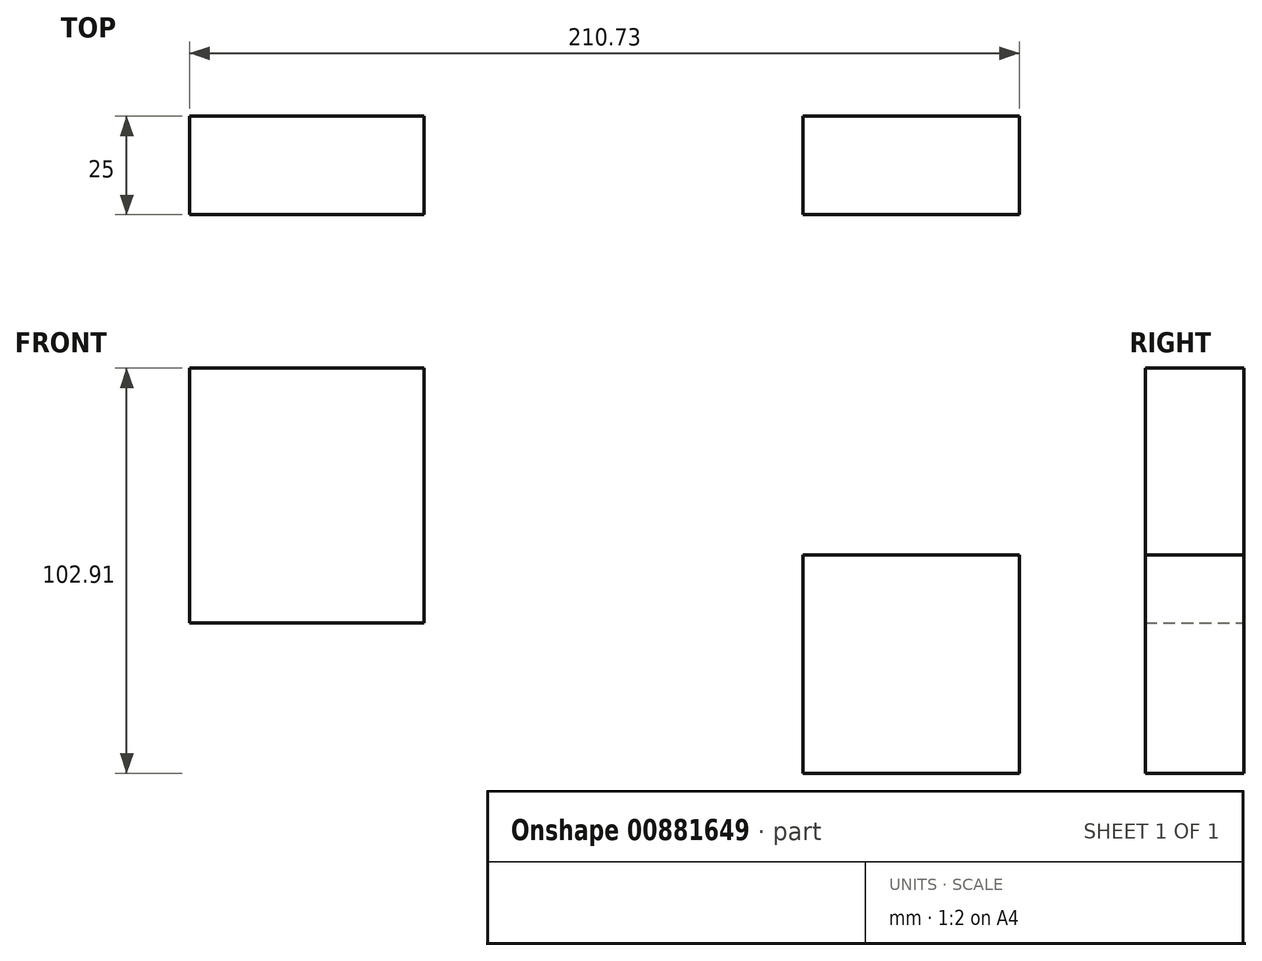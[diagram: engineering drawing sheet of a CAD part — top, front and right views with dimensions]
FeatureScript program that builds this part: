
annotation { "Feature Type Name" : "Feature", "Feature Type Description" : "" }
export const myFeature = defineFeature(function(context is Context, id is Id, definition is map)
    precondition{}
    {
        {
            var Q0;
            Q0=qCreatedBy(makeId("Front.planeOp"),FACE);
            var sketch = newSketch(context, id + "F0", { "sketchPlane" : qUnion([Q0])});
            skLineSegment(sketch, "E0.bottom", {"start": v(-190.64, 25.87) * mm, "end": v(-131.1, 25.87) * mm});
            skLineSegment(sketch, "E0.top", {"start": v(-190.64, 90.62) * mm, "end": v(-131.1, 90.62) * mm});
            skLineSegment(sketch, "E0.left", {"start": v(-190.64, 25.87) * mm, "end": v(-190.64, 90.62) * mm});
            skLineSegment(sketch, "E0.right", {"start": v(-131.1, 25.87) * mm, "end": v(-131.1, 90.62) * mm});
            skPoint(sketch, "E0.middle", {"position": v(-160.87, 58.25) * mm});
            skLineSegment(sketch, "E1.bottom", {"start": v(-34.83, -12.29) * mm, "end": v(20.1, -12.29) * mm});
            skLineSegment(sketch, "E1.top", {"start": v(-34.83, 43.22) * mm, "end": v(20.1, 43.22) * mm});
            skLineSegment(sketch, "E1.left", {"start": v(-34.83, -12.29) * mm, "end": v(-34.83, 43.22) * mm});
            skLineSegment(sketch, "E1.right", {"start": v(20.1, -12.29) * mm, "end": v(20.1, 43.22) * mm});
            skPoint(sketch, "E1.middle", {"position": v(-7.37, 15.47) * mm});
            skSolve(sketch);
        }
        {
            var Q0;
            Q0=makeQuery(id+"F0.imprint","IMPRINT",FACE,{"disambiguationData":[TD([[makeQuery(id+"F0.imprint","IMPRINT",EDGE,{"derivedFrom":sQuery(id+"F0.wireOp",EDGE,"E0.bottom")}),1.0]])]});
            var Q1;
            Q1=makeQuery(id+"F0.imprint","IMPRINT",FACE,{"disambiguationData":[TD([[makeQuery(id+"F0.imprint","IMPRINT",EDGE,{"derivedFrom":sQuery(id+"F0.wireOp",EDGE,"E1.bottom")}),1.0]])]});
            extrude(context, id + "F1", {"entities" : qUnion([Q0, Q1]), "depth" : 25 * mm, "offsetDistance" : 25 * mm});
        }
    });
